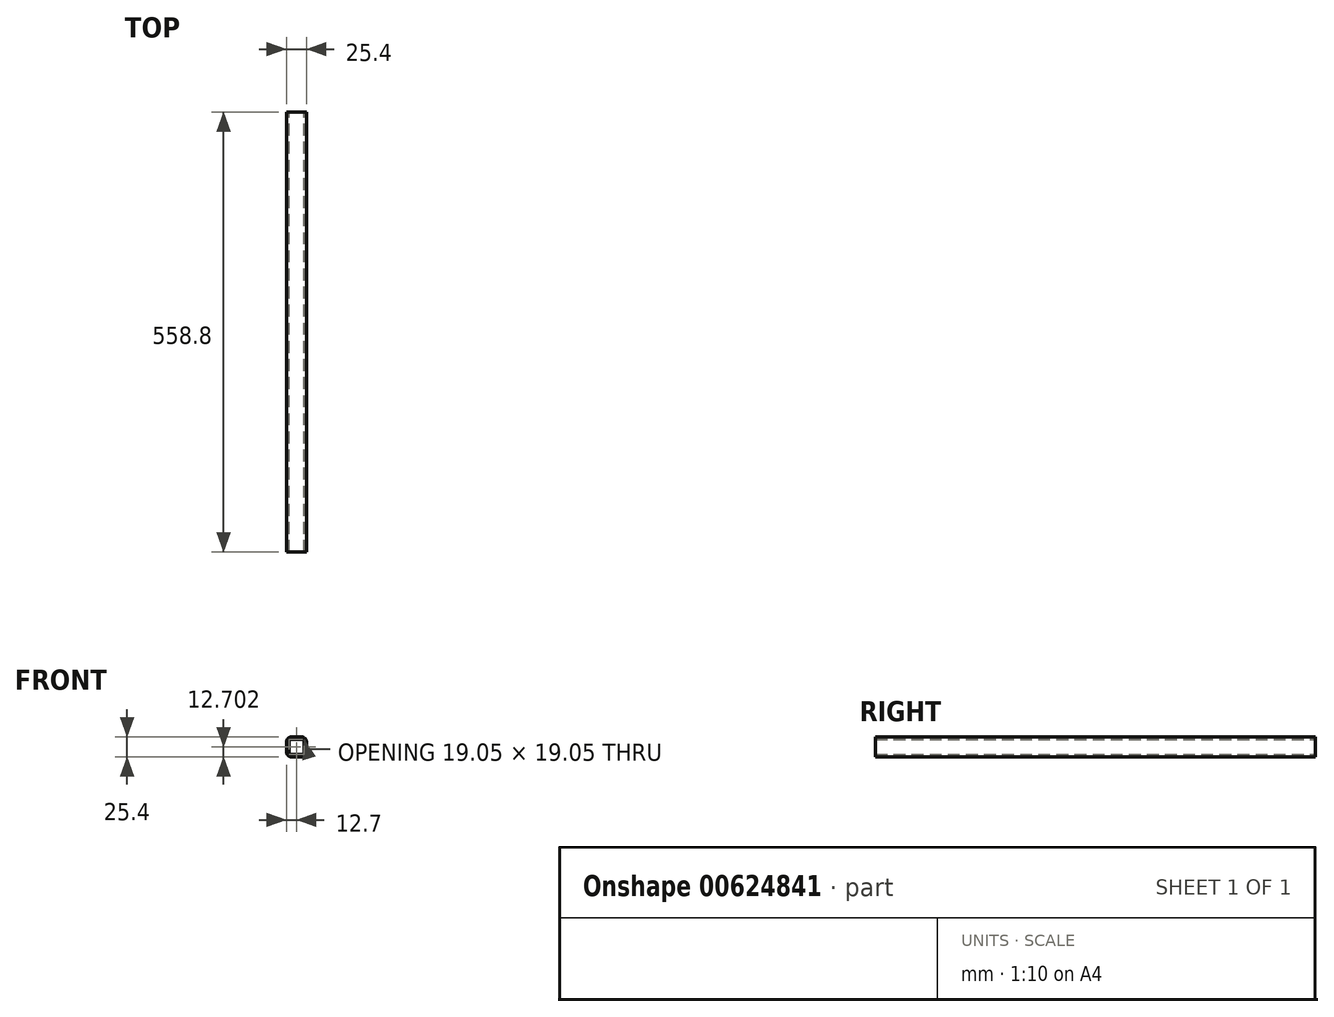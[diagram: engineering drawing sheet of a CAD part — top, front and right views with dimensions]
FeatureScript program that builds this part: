
annotation { "Feature Type Name" : "Feature", "Feature Type Description" : "" }
export const myFeature = defineFeature(function(context is Context, id is Id, definition is map)
    precondition{}
    {
        {
            var Q0;
            Q0=qCreatedBy(makeId("Front.planeOp"),FACE);
            var sketch = newSketch(context, id + "F0", { "sketchPlane" : qUnion([Q0])});
            skLineSegment(sketch, "E0.bottom", {"start": v(-6.35, 13.31) * mm, "end": v(6.35, 13.31) * mm});
            skLineSegment(sketch, "E0.top", {"start": v(-6.35, -12.09) * mm, "end": v(6.35, -12.09) * mm});
            skLineSegment(sketch, "E0.left", {"start": v(-12.7, 6.96) * mm, "end": v(-12.7, -5.74) * mm});
            skLineSegment(sketch, "E0.right", {"start": v(12.7, 6.96) * mm, "end": v(12.7, -5.74) * mm});
            skPoint(sketch, "E0.middle", {"position": v(0, 0.61) * mm});
            skPoint(sketch, "E1.visualSharp", {"position": v(-12.7, 13.31) * mm});
            skArc(sketch, "E1.filletArc", {"start": v(-11.77, 10.28) * mm, "mid": v(-12.46, 8.68) * mm, "end": v(-12.7, 6.96) * mm});
            skPoint(sketch, "E2.visualSharp", {"position": v(-6.35, 13.31) * mm});
            skArc(sketch, "E2.filletArc", {"start": v(-6.35, 13.31) * mm, "mid": v(-9.45, 12.5) * mm, "end": v(-11.77, 10.28) * mm});
            skPoint(sketch, "E3.visualSharp", {"position": v(12.7, 13.31) * mm});
            skArc(sketch, "E3.filletArc", {"start": v(12.7, 6.96) * mm, "mid": v(10.84, 11.45) * mm, "end": v(6.35, 13.31) * mm});
            skPoint(sketch, "E4.visualSharp", {"position": v(12.7, -12.09) * mm});
            skArc(sketch, "E4.filletArc", {"start": v(6.35, -12.09) * mm, "mid": v(10.84, -10.23) * mm, "end": v(12.7, -5.74) * mm});
            skPoint(sketch, "E5.visualSharp", {"position": v(-12.7, -12.09) * mm});
            skArc(sketch, "E5.filletArc", {"start": v(-12.7, -5.74) * mm, "mid": v(-10.84, -10.23) * mm, "end": v(-6.35, -12.09) * mm});
            skLineSegment(sketch, "E6.0", {"start": v(-9.52, 6.96) * mm, "end": v(-9.53, -5.74) * mm});
            skArc(sketch, "E6.1", {"start": v(-9.53, -5.74) * mm, "mid": v(-8.6, -7.98) * mm, "end": v(-6.35, -8.91) * mm});
            skLineSegment(sketch, "E6.2", {"start": v(-6.35, -8.91) * mm, "end": v(6.35, -8.91) * mm});
            skArc(sketch, "E6.3", {"start": v(6.35, -8.91) * mm, "mid": v(8.6, -7.98) * mm, "end": v(9.52, -5.74) * mm});
            skArc(sketch, "E6.4", {"start": v(-6.35, 10.14) * mm, "mid": v(-8.6, 9.2) * mm, "end": v(-9.52, 6.96) * mm});
            skLineSegment(sketch, "E6.5", {"start": v(-6.35, 10.14) * mm, "end": v(6.35, 10.14) * mm});
            skArc(sketch, "E6.6", {"start": v(9.53, 6.96) * mm, "mid": v(8.6, 9.2) * mm, "end": v(6.35, 10.14) * mm});
            skLineSegment(sketch, "E6.7", {"start": v(9.53, 6.96) * mm, "end": v(9.52, -5.74) * mm});
            skSolve(sketch);
        }
        {
            var Q0;
            Q0=qSketchRegion(id+"F0",true);
            extrude(context, id + "F1", {"entities" : qUnion([Q0]), "endBound" : BoundingType.SYMMETRIC, "depth" : 558.8 * mm, "offsetDistance" : 25.4 * mm});
        }
    });
